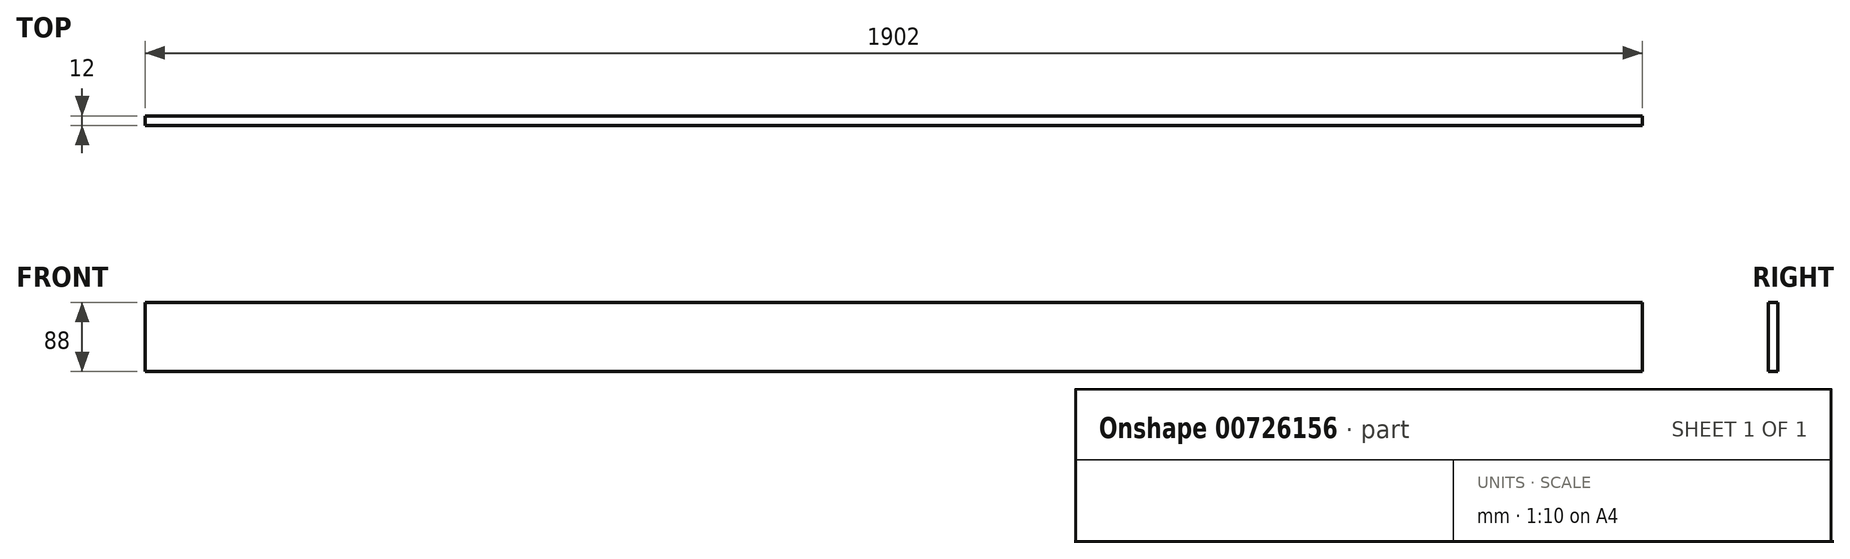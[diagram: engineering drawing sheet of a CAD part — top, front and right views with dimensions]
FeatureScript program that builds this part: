
annotation { "Feature Type Name" : "Feature", "Feature Type Description" : "" }
export const myFeature = defineFeature(function(context is Context, id is Id, definition is map)
    precondition{}
    {
        {
            var Q0;
            Q0=qCreatedBy(makeId("Front.planeOp"),FACE);
            var sketch = newSketch(context, id + "F0", { "sketchPlane" : qUnion([Q0])});
            skLineSegment(sketch, "E0.bottom", {"start": v(-951, 44) * mm, "end": v(951, 44) * mm});
            skLineSegment(sketch, "E0.top", {"start": v(-951, -44) * mm, "end": v(951, -44) * mm});
            skLineSegment(sketch, "E0.left", {"start": v(-951, 44) * mm, "end": v(-951, -44) * mm});
            skLineSegment(sketch, "E0.right", {"start": v(951, 44) * mm, "end": v(951, -44) * mm});
            skLineSegment(sketch, "E1", {"start": v(0, 44) * mm, "end": v(0, -44) * mm, "construction": true});
            skSolve(sketch);
        }
        {
            var Q0;
            Q0 = qSketchRegion(id + "F0", true);
            extrude(context, id + "F1", {"entities" : qUnion([Q0]), "depth" : 12 * mm, "offsetDistance" : 25 * mm});
        }
    });
